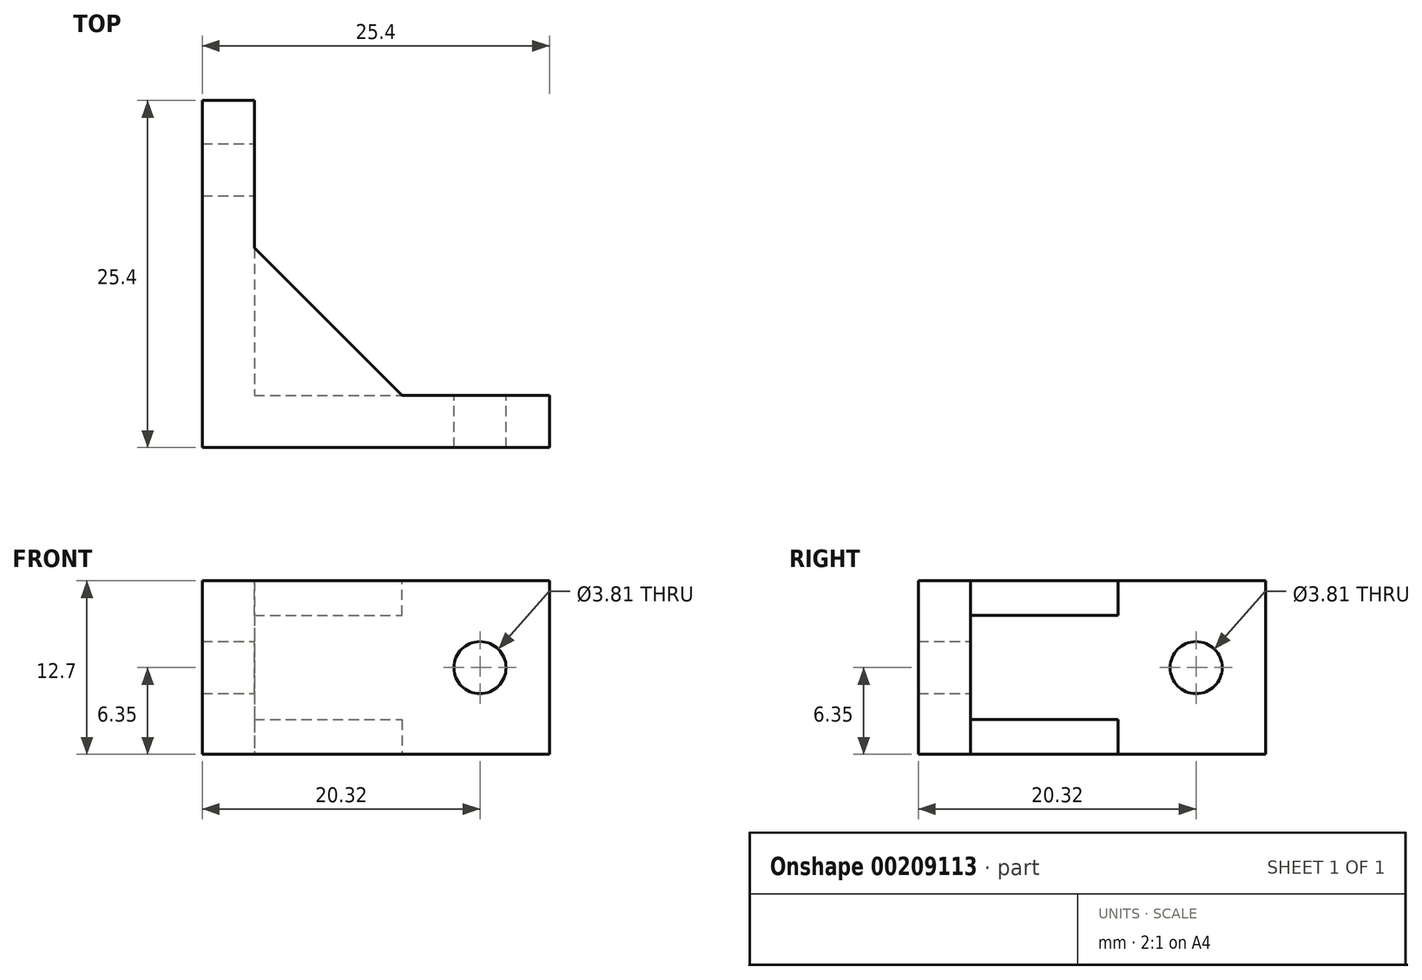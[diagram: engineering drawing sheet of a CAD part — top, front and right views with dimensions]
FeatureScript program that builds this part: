
annotation { "Feature Type Name" : "Feature", "Feature Type Description" : "" }
export const myFeature = defineFeature(function(context is Context, id is Id, definition is map)
    precondition{}
    {
        {
            var Q0;
            Q0=qCreatedBy(makeId("Top.planeOp"),FACE);
            var sketch = newSketch(context, id + "F0", { "sketchPlane" : qUnion([Q0])});
            skLineSegment(sketch, "E0", {"start": v(0, 0) * mm, "end": v(0, 25.4) * mm});
            skLineSegment(sketch, "E1", {"start": v(0, 0) * mm, "end": v(25.4, 0) * mm});
            skLineSegment(sketch, "E2", {"start": v(25.4, 0) * mm, "end": v(25.4, 3.81) * mm});
            skLineSegment(sketch, "E3", {"start": v(0, 25.4) * mm, "end": v(3.81, 25.4) * mm});
            skLineSegment(sketch, "E4", {"start": v(3.81, 25.4) * mm, "end": v(3.81, 3.8) * mm});
            skLineSegment(sketch, "E5", {"start": v(3.81, 3.8) * mm, "end": v(25.4, 3.81) * mm});
            skSolve(sketch);
        }
        {
            var Q0;
            Q0 = qSketchRegion(id + "F0", true);
            extrude(context, id + "F1", {"entities" : qUnion([Q0]), "depth" : 12.7 * mm});
        }
        {
            var Q0;
            Q0=makeQuery(id+"F1.opExtrude","CAP_FACE",FACE,{"disambiguationData":[OSD([sQuery(id+"F0.wireOp",EDGE,"E0"),sQuery(id+"F0.wireOp",EDGE,"E1"),sQuery(id+"F0.wireOp",EDGE,"E2"),sQuery(id+"F0.wireOp",EDGE,"E3"),sQuery(id+"F0.wireOp",EDGE,"E4"),sQuery(id+"F0.wireOp",EDGE,"E5")])],"isStart":false});
            var sketch = newSketch(context, id + "F2", { "sketchPlane" : qUnion([Q0])});
            skLineSegment(sketch, "E6", {"start": v(3.81, 14.6) * mm, "end": v(14.6, 3.8) * mm});
            skLineSegment(sketch, "E7", {"start": v(14.6, 3.8) * mm, "end": v(3.81, 3.8) * mm});
            skLineSegment(sketch, "E8", {"start": v(3.81, 3.8) * mm, "end": v(3.81, 14.6) * mm});
            skSolve(sketch);
        }
        {
            var Q0;
            Q0=qCreatedBy(makeId("Right.planeOp"),FACE);
            var sketch = newSketch(context, id + "F3", { "sketchPlane" : qUnion([Q0])});
            skSolve(sketch);
        }
        {
            var Q0;
            Q0 = qSketchRegion(id + "F3", true);
            var Q1;
            Q1=makeQuery(id+"F2.imprint","IMPRINT",FACE,{"disambiguationData":[TD([[makeQuery(id+"F2.imprint","IMPRINT",EDGE,{"derivedFrom":sQuery(id+"F2.wireOp",EDGE,"E6")}),-1.0]])]});
            extrude(context, id + "F4", {"entities" : qUnion([Q0, Q1]), "operationType" : NewBodyOperationType.ADD, "oppositeDirection" : true, "depth" : 2.54 * mm});
        }
        {
            var Q0;
            Q0=makeQuery(id+"F1.opExtrude","CAP_FACE",FACE,{"disambiguationData":[OSD([sQuery(id+"F0.wireOp",EDGE,"E0"),sQuery(id+"F0.wireOp",EDGE,"E1"),sQuery(id+"F0.wireOp",EDGE,"E2"),sQuery(id+"F0.wireOp",EDGE,"E3"),sQuery(id+"F0.wireOp",EDGE,"E4"),sQuery(id+"F0.wireOp",EDGE,"E5")])],"isStart":true});
            var sketch = newSketch(context, id + "F5", { "sketchPlane" : qUnion([Q0])});
            skLineSegment(sketch, "E9", {"start": v(14.6, -3.8) * mm, "end": v(3.81, -14.6) * mm});
            skLineSegment(sketch, "E10", {"start": v(3.81, -14.6) * mm, "end": v(3.81, -3.8) * mm});
            skLineSegment(sketch, "E11", {"start": v(3.81, -3.8) * mm, "end": v(14.6, -3.8) * mm});
            skSolve(sketch);
        }
        {
            var Q0;
            Q0=makeQuery(id+"F1.opExtrude","SWEPT_FACE",FACE,{"disambiguationData":[OSD([sQuery(id+"F0.wireOp",EDGE,"E4")])]});
            var sketch = newSketch(context, id + "F6", { "sketchPlane" : qUnion([Q0])});
            skCircle(sketch, "E12", {"center": v(20.32, 6.35) * mm, "radius": 1.9 * mm});
            skSolve(sketch);
        }
        {
            var Q0;
            Q0=makeQuery(id+"F6.imprint","IMPRINT",FACE,{"disambiguationData":[TD([[makeQuery(id+"F6.imprint","IMPRINT",EDGE,{"derivedFrom":sQuery(id+"F6.wireOp",EDGE,"E12")}),1.0]])]});
            extrude(context, id + "F7", {"entities" : qUnion([Q0]), "operationType" : NewBodyOperationType.REMOVE, "oppositeDirection" : true, "depth" : 25.4 * mm});
        }
        {
            var Q0;
            Q0=makeQuery(id+"F5.imprint","IMPRINT",FACE,{"disambiguationData":[TD([[makeQuery(id+"F5.imprint","IMPRINT",EDGE,{"derivedFrom":sQuery(id+"F5.wireOp",EDGE,"E9")}),-1.0]])]});
            extrude(context, id + "F8", {"entities" : qUnion([Q0]), "operationType" : NewBodyOperationType.ADD, "oppositeDirection" : true, "depth" : 2.54 * mm});
        }
        {
            var Q0;
            Q0=makeQuery(id+"F1.opExtrude","SWEPT_FACE",FACE,{"disambiguationData":[OSD([sQuery(id+"F0.wireOp",EDGE,"E5")])]});
            var sketch = newSketch(context, id + "F9", { "sketchPlane" : qUnion([Q0])});
            skCircle(sketch, "E13", {"center": v(-20.32, 6.35) * mm, "radius": 1.9 * mm});
            skSolve(sketch);
        }
        {
            var Q0;
            Q0=makeQuery(id+"F9.imprint","IMPRINT",FACE,{"disambiguationData":[TD([[makeQuery(id+"F9.imprint","IMPRINT",EDGE,{"derivedFrom":sQuery(id+"F9.wireOp",EDGE,"E13")}),1.0]])]});
            extrude(context, id + "F10", {"entities" : qUnion([Q0]), "operationType" : NewBodyOperationType.REMOVE, "oppositeDirection" : true, "depth" : 25.4 * mm});
        }
    });
